# Revit family: Seating-LAMMHULTS-PORTUS-Easy_Chair-High_Back
name_source: partatom
category: Furniture
revit_build: Autodesk Revit 2014 (Build: 20140709_2115(x64)
units: mm (PartAtom-declared; Revit-internal decimal feet)

## types (4) — shared parameters
Assembly Code = E2020
Description = *Please enter mtrl description here for use in mto*
Keynote = 46.B
Manufacturer = LAMMHULTS
Model = PORTUS
URL = www.lammhults.se
Weight = 50 kg

## per-type parameters (varying)
| type | Back Material | Legs Material | Seat Material | Steel Legs | Wood Legs |
| 1 Colour Steel legs | Fabric -  Blue Woven | Metal - Chrome - Polished | Fabric -  Blue Woven | Yes | No |
| 1 Colour Wood legs | Fabric -  Blue Woven | Wood - Solid - Ashtree | Fabric -  Blue Woven | No | Yes |
| 2 Colour Steel legs | Fabric - Dark Purple Woven | Metal - Chrome - Polished | Fabric - Light Beige Woven | Yes | No |
| 2 Colour Wood legs | Fabric - Dark Purple Woven | Wood - Solid - Ashtree | Fabric - Light Beige Woven | No | Yes |

## geometry (parser evidence)
native form markers: Blend x12, Sweep x2
no freeform markers — native parametric forms only
